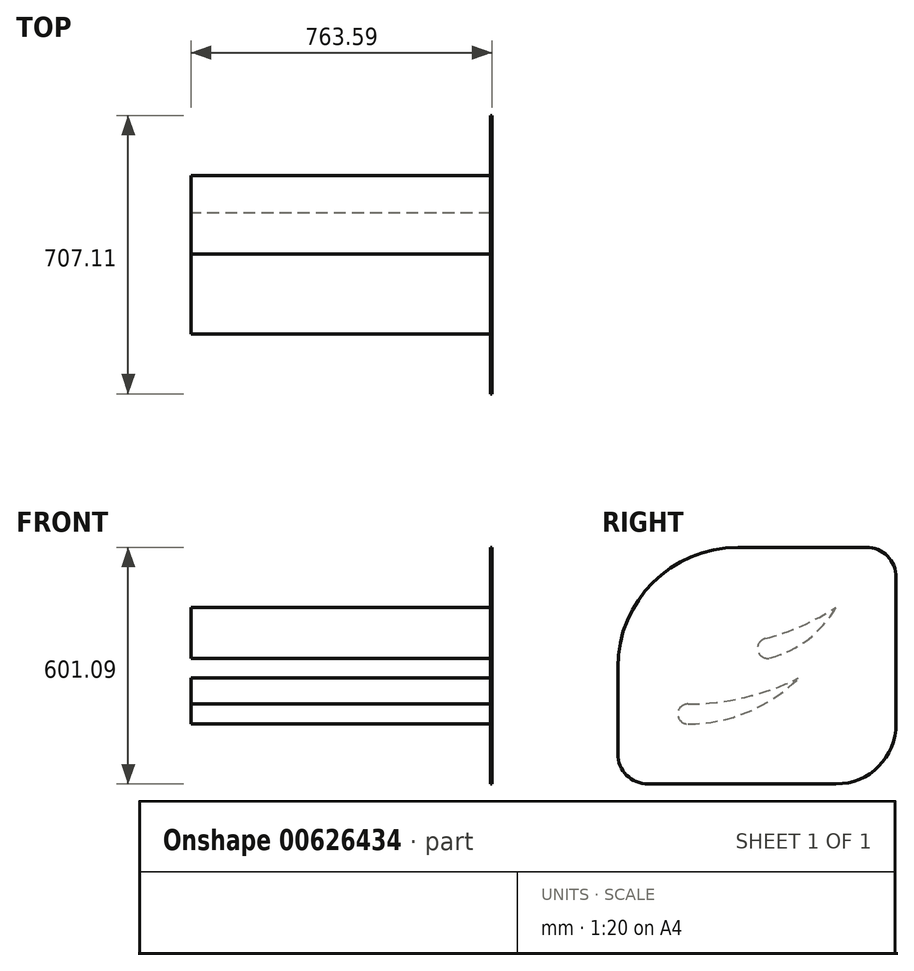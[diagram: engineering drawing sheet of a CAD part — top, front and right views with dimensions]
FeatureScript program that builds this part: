
annotation { "Feature Type Name" : "Feature", "Feature Type Description" : "" }
export const myFeature = defineFeature(function(context is Context, id is Id, definition is map)
    precondition{}
    {
        {
            var Q0;
            Q0=qCreatedBy(makeId("Right.planeOp"),FACE);
            var sketch = newSketch(context, id + "F0", { "sketchPlane" : qUnion([Q0])});
            skArc(sketch, "E0", {"start": v(0, -398.24) * mm, "mid": v(152.4, -367.93) * mm, "end": v(281.6, -281.6) * mm});
            skArc(sketch, "E1", {"start": v(0, -398.24) * mm, "mid": v(-25.4, -372.84) * mm, "end": v(0, -347.44) * mm});
            skArc(sketch, "E2", {"start": v(0, -347.44) * mm, "mid": v(144.6, -330.76) * mm, "end": v(281.6, -281.6) * mm});
            skSolve(sketch);
        }
        {
            var Q0;
            Q0=makeQuery(id+"F0.imprint","IMPRINT",FACE,{"disambiguationData":[TD([[makeQuery(id+"F0.imprint","IMPRINT",EDGE,{"derivedFrom":sQuery(id+"F0.wireOp",EDGE,"E0")}),1.0]])]});
            extrude(context, id + "F1", {"entities" : qUnion([Q0]), "depth" : 762 * mm, "offsetDistance" : 25.4 * mm});
        }
        {
            var Q0;
            Q0=qCreatedBy(makeId("Right.planeOp"),FACE);
            var sketch = newSketch(context, id + "F2", { "sketchPlane" : qUnion([Q0])});
            skArc(sketch, "E3", {"start": v(209.28, -230.58) * mm, "mid": v(305.89, -182.94) * mm, "end": v(376.9, -101.95) * mm});
            skArc(sketch, "E4", {"start": v(209.28, -230.58) * mm, "mid": v(178.17, -212.62) * mm, "end": v(196.13, -181.5) * mm});
            skArc(sketch, "E5", {"start": v(196.13, -181.5) * mm, "mid": v(289.56, -148.65) * mm, "end": v(376.9, -101.95) * mm});
            skSolve(sketch);
        }
        {
            var Q0;
            Q0 = qSketchRegion(id + "F2", true);
            extrude(context, id + "F3", {"entities" : qUnion([Q0]), "depth" : 762 * mm, "offsetDistance" : 25.4 * mm});
        }
        {
            var Q0;
            Q0=makeQuery(id+"F1.opExtrude","CAP_FACE",FACE,{"disambiguationData":[OSD([sQuery(id+"F0.wireOp",EDGE,"E0"),sQuery(id+"F0.wireOp",EDGE,"E1"),sQuery(id+"F0.wireOp",EDGE,"E2")])],"isStart":false});
            var sketch = newSketch(context, id + "F4", { "sketchPlane" : qUnion([Q0])});
            skLineSegment(sketch, "E6.bottom", {"start": v(-177.8, -550.64) * mm, "end": v(529.3, -550.64) * mm});
            skLineSegment(sketch, "E6.top", {"start": v(-177.8, 50.45) * mm, "end": v(529.3, 50.45) * mm});
            skLineSegment(sketch, "E6.left", {"start": v(-177.8, -550.64) * mm, "end": v(-177.8, 50.45) * mm});
            skLineSegment(sketch, "E6.right", {"start": v(529.3, -550.64) * mm, "end": v(529.3, 50.45) * mm});
            skSolve(sketch);
        }
        {
            var Q0;
            Q0=makeQuery(id+"F4.imprint","IMPRINT",FACE,{"disambiguationData":[TD([[makeQuery(id+"F4.imprint","IMPRINT",EDGE,{"derivedFrom":sQuery(id+"F4.wireOp",EDGE,"E6.bottom")}),1.0]])]});
            var Q1;
            Q1=makeQuery(id+"F4.imprint","IMPRINT",FACE,{"disambiguationData":[TD([[makeQuery(id+"F4.imprint","IMPRINT",EDGE,{"derivedFrom":makeQuery(id+"F1.opExtrude","CAP_EDGE",EDGE,{"disambiguationData":[OSD([sQuery(id+"F0.wireOp",EDGE,"E0")])],"isStart":false})}),1.0]])]});
            extrude(context, id + "F5", {"entities" : qUnion([Q0, Q1]), "operationType" : NewBodyOperationType.ADD, "endBound" : BoundingType.SYMMETRIC, "depth" : 3.17 * mm, "offsetDistance" : 25.4 * mm});
        }
        {
            var Q0;
            Q0=makeQuery(id+"F5.opExtrude","SWEPT_EDGE",EDGE,{"disambiguationData":[OSD([sQuery(id+"F4.wireOp",EDGE,"E6.top"),sQuery(id+"F4.wireOp",EDGE,"E6.left")])]});
            fillet(context, id + "F6", {"entities" : qUnion([Q0]), "radius" : 304.8 * mm, "tangentPropagation" : true, "allowEdgeOverflow" : false});
        }
        {
            var Q0;
            Q0=makeQuery(id+"F5.opExtrude","SWEPT_EDGE",EDGE,{"disambiguationData":[OSD([sQuery(id+"F4.wireOp",EDGE,"E6.bottom"),sQuery(id+"F4.wireOp",EDGE,"E6.left")])]});
            var Q1;
            Q1=makeQuery(id+"F5.opExtrude","SWEPT_EDGE",EDGE,{"disambiguationData":[OSD([sQuery(id+"F4.wireOp",EDGE,"E6.top"),sQuery(id+"F4.wireOp",EDGE,"E6.right")])]});
            fillet(context, id + "F7", {"entities" : qUnion([Q0, Q1]), "radius" : 76.2 * mm, "tangentPropagation" : true, "allowEdgeOverflow" : false});
        }
        {
            var Q0;
            Q0=makeQuery(id+"F5.opExtrude","SWEPT_EDGE",EDGE,{"disambiguationData":[OSD([sQuery(id+"F4.wireOp",EDGE,"E6.bottom"),sQuery(id+"F4.wireOp",EDGE,"E6.right")])]});
            fillet(context, id + "F8", {"entities" : qUnion([Q0]), "radius" : 152.4 * mm, "tangentPropagation" : true, "allowEdgeOverflow" : false});
        }
    });
